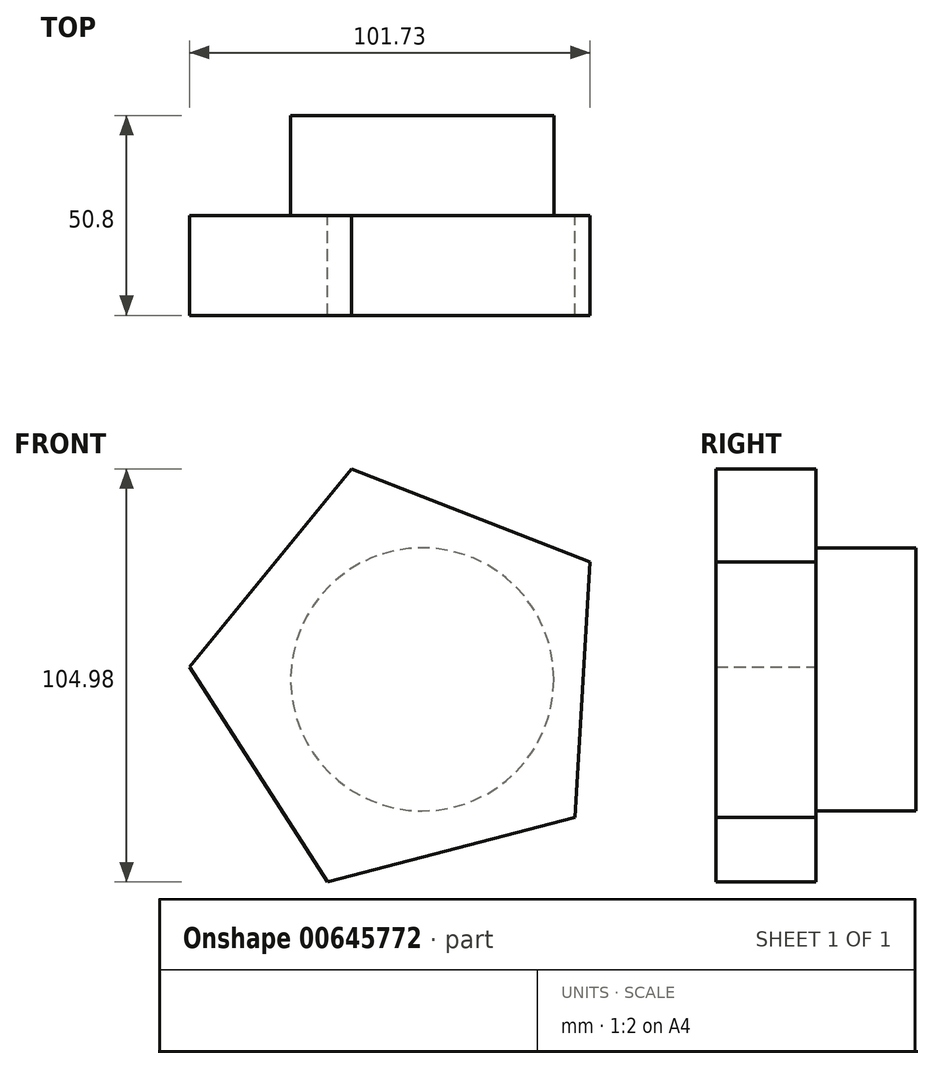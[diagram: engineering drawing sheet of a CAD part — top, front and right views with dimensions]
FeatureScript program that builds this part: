
annotation { "Feature Type Name" : "Feature", "Feature Type Description" : "" }
export const myFeature = defineFeature(function(context is Context, id is Id, definition is map)
    precondition{}
    {
        {
            var Q0;
            Q0=qCreatedBy(makeId("Front.planeOp"),FACE);
            var sketch = newSketch(context, id + "F0", { "sketchPlane" : qUnion([Q0])});
            skCircle(sketch, "E0", {"center": v(0, 0) * mm, "radius": 33.43 * mm});
            skSolve(sketch);
        }
        {
            var Q0;
            Q0=makeQuery(id+"F0.imprint","IMPRINT",FACE,{"disambiguationData":[TD([[makeQuery(id+"F0.imprint","IMPRINT",EDGE,{"derivedFrom":sQuery(id+"F0.wireOp",EDGE,"E0")}),1.0]])]});
            extrude(context, id + "F1", {"entities" : qUnion([Q0]), "depth" : 25.4 * mm, "offsetDistance" : 25.4 * mm});
        }
        {
            var Q0;
            Q0=makeQuery(id+"F1.opExtrude","CAP_FACE",FACE,{"disambiguationData":[OSD([sQuery(id+"F0.wireOp",EDGE,"E0")])],"isStart":false});
            var sketch = newSketch(context, id + "F2", { "sketchPlane" : qUnion([Q0])});
            skCircle(sketch, "E1.cCircle", {"center": v(-3.93, 0) * mm, "radius": 44.72 * mm, "construction": true});
            skLineSegment(sketch, "E1.0", {"start": v(-59.11, 3.23) * mm, "end": v(-17.9, 53.49) * mm});
            skLineSegment(sketch, "E1.1", {"start": v(-17.9, 53.49) * mm, "end": v(42.62, 29.82) * mm});
            skLineSegment(sketch, "E1.2", {"start": v(42.62, 29.82) * mm, "end": v(38.82, -35.05) * mm});
            skLineSegment(sketch, "E1.3", {"start": v(38.82, -35.05) * mm, "end": v(-24.06, -51.49) * mm});
            skLineSegment(sketch, "E1.4", {"start": v(-24.06, -51.49) * mm, "end": v(-59.11, 3.23) * mm});
            skPoint(sketch, "E1.0.midPoint", {"position": v(-38.51, 28.36) * mm});
            skSolve(sketch);
        }
        {
            var Q0;
            Q0 = qSketchRegion(id + "F2", true);
            extrude(context, id + "F3", {"entities" : qUnion([Q0]), "operationType" : NewBodyOperationType.ADD, "depth" : 25.4 * mm, "offsetDistance" : 25.4 * mm});
        }
    });
